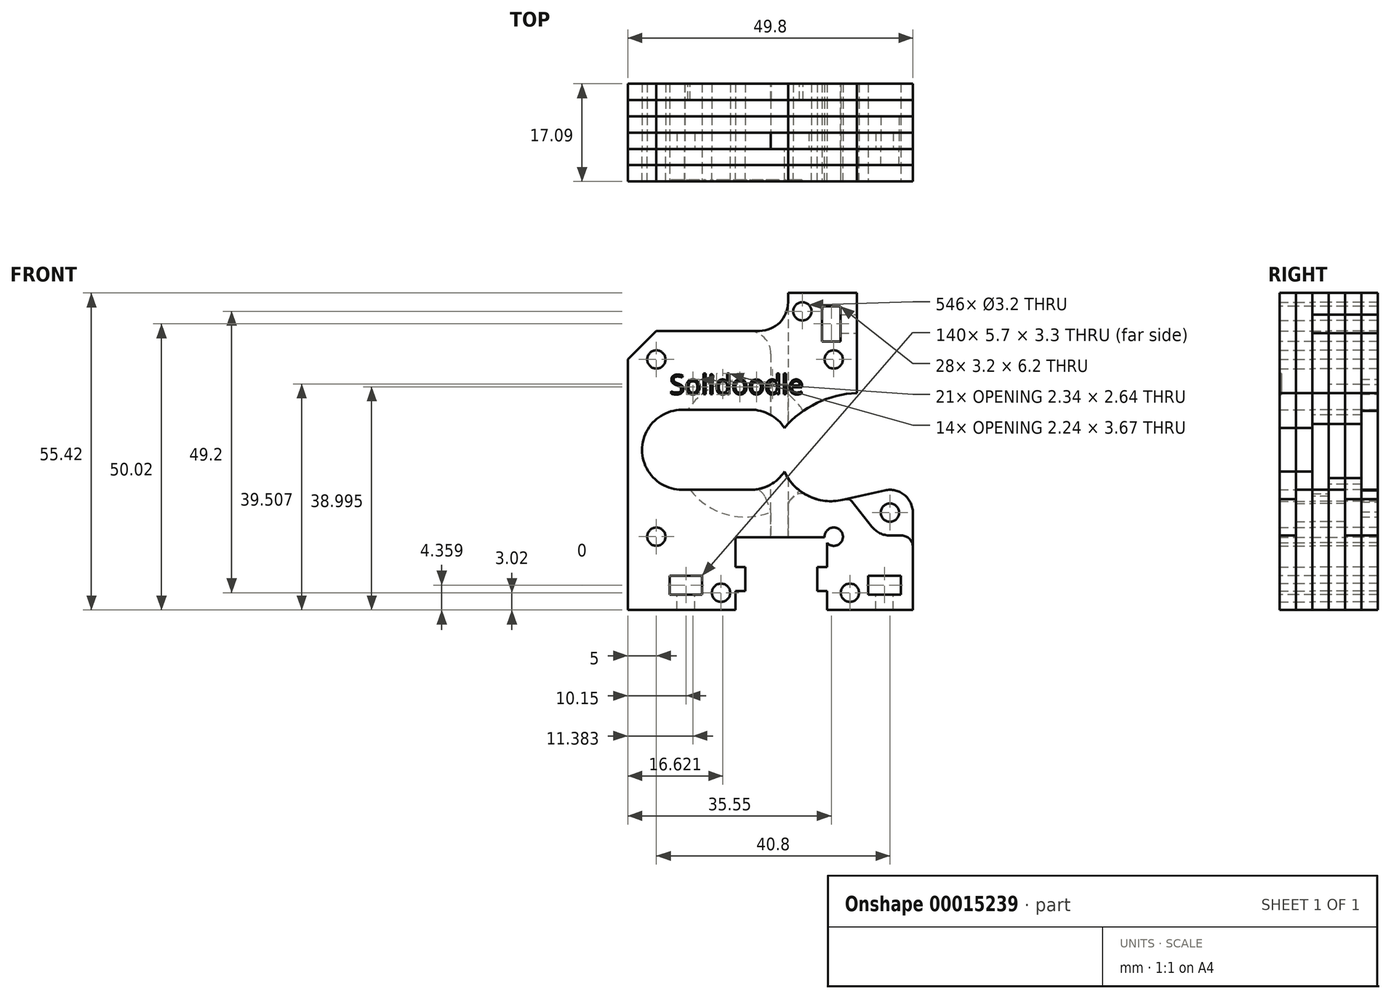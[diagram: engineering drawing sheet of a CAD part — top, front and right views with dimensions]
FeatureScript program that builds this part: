
annotation { "Feature Type Name" : "Feature", "Feature Type Description" : "" }
export const myFeature = defineFeature(function(context is Context, id is Id, definition is map)
    precondition{}
    {
        {
            var Q0;
            Q0=qCreatedBy(makeId("Front.planeOp"),FACE);
            var sketch = newSketch(context, id + "F0", { "sketchPlane" : qUnion([Q0])});
            skLineSegment(sketch, "E0.rect.left", {"start": v(-24.9, 13.58) * mm, "end": v(-24.9, -30.22) * mm});
            skLineSegment(sketch, "E0.rect.right", {"start": v(24.9, -13.2) * mm, "end": v(24.9, -30.2) * mm});
            skPoint(sketch, "E0.rect.middle", {"position": v(0, 0) * mm});
            skPoint(sketch, "E1", {"position": v(-15.4, -2.22) * mm});
            skArc(sketch, "E2", {"start": v(-15, 4.77) * mm, "mid": v(-22.4, -2.27) * mm, "end": v(-14.9, -9.2) * mm});
            skPoint(sketch, "E3", {"position": v(-3.4, -2.2) * mm});
            skArc(sketch, "E4", {"start": v(-3.4, -9.2) * mm, "mid": v(-0.07, -8.36) * mm, "end": v(2.46, -6.03) * mm});
            skLineSegment(sketch, "E5", {"start": v(-15, 4.77) * mm, "end": v(-3.4, 4.8) * mm});
            skLineSegment(sketch, "E6", {"start": v(-3.4, -9.2) * mm, "end": v(-14.9, -9.2) * mm});
            skPoint(sketch, "E7", {"position": v(10.6, -2.2) * mm});
            skArc(sketch, "E8", {"start": v(2.46, -6.03) * mm, "mid": v(6.65, -10.29) * mm, "end": v(12.58, -10.98) * mm});
            skArc(sketch, "E9.trimOffspring", {"start": v(2.46, 1.63) * mm, "mid": v(-0.09, 3.97) * mm, "end": v(-3.44, 4.8) * mm});
            skPoint(sketch, "E10", {"position": v(20.9, -13.2) * mm});
            skCircle(sketch, "E11", {"center": v(20.9, -13.2) * mm, "radius": 1.6 * mm});
            skPoint(sketch, "E12", {"position": v(24.9, -13.2) * mm});
            skLineSegment(sketch, "E13", {"start": v(15.1, 25.2) * mm, "end": v(3.1, 25.2) * mm});
            skLineSegment(sketch, "E14", {"start": v(3.1, 25.2) * mm, "end": v(3.1, 18.58) * mm});
            skLineSegment(sketch, "E15", {"start": v(3.1, 18.58) * mm, "end": v(-19.9, 18.58) * mm});
            skLineSegment(sketch, "E16.0", {"start": v(15.1, 25.2) * mm, "end": v(15.1, 7.71) * mm});
            skCircle(sketch, "E17", {"center": v(-19.9, 13.58) * mm, "radius": 1.6 * mm});
            skCircle(sketch, "E18", {"center": v(11.09, 13.58) * mm, "radius": 1.6 * mm});
            skCircle(sketch, "E19", {"center": v(-19.9, -17.4) * mm, "radius": 1.6 * mm});
            skArc(sketch, "E20", {"start": v(9.9, -18.48) * mm, "mid": v(12.56, -16.79) * mm, "end": v(9.5, -17.5) * mm});
            skCircle(sketch, "E21", {"center": v(20.9, -13.2) * mm, "radius": 4 * mm, "construction": true});
            skLineSegment(sketch, "E22", {"start": v(12.58, -10.98) * mm, "end": v(20.02, -9.3) * mm});
            skArc(sketch, "E23", {"start": v(20.02, -9.3) * mm, "mid": v(23.4, -10.08) * mm, "end": v(24.9, -13.2) * mm});
            skPoint(sketch, "E24", {"position": v(-19.9, 18.58) * mm});
            skPoint(sketch, "E25", {"position": v(-24.9, 13.58) * mm});
            skLineSegment(sketch, "E26", {"start": v(-19.9, 18.58) * mm, "end": v(-24.9, 13.58) * mm});
            skPoint(sketch, "E27.orphan", {"position": v(-24.9, 18.58) * mm});
            skPoint(sketch, "E28", {"position": v(-6.1, -30.2) * mm});
            skPoint(sketch, "E29", {"position": v(9.9, -30.2) * mm});
            skPoint(sketch, "E30.visualSharp", {"position": v(2.46, 1.63) * mm});
            skPoint(sketch, "E31.visualSharp", {"position": v(2.46, -6.03) * mm});
            skLineSegment(sketch, "E32", {"start": v(-6.1, -30.2) * mm, "end": v(-6.1, -26.9) * mm});
            skLineSegment(sketch, "E33", {"start": v(-6.1, -26.9) * mm, "end": v(-4.39, -26.9) * mm});
            skLineSegment(sketch, "E34", {"start": v(-4.39, -26.9) * mm, "end": v(-4.39, -22.7) * mm});
            skLineSegment(sketch, "E35", {"start": v(-4.39, -22.7) * mm, "end": v(-6.1, -22.7) * mm});
            skLineSegment(sketch, "E36", {"start": v(-6.1, -22.7) * mm, "end": v(-6.1, -17.5) * mm});
            skLineSegment(sketch, "E37", {"start": v(-6.1, -17.5) * mm, "end": v(1.9, -17.5) * mm});
            skLineSegment(sketch, "E38", {"start": v(1.9, -30.2) * mm, "end": v(1.9, -17.5) * mm, "construction": true});
            skLineSegment(sketch, "E39.MirrorCS", {"start": v(9.5, -17.5) * mm, "end": v(1.9, -17.5) * mm});
            skLineSegment(sketch, "E40.MirrorCS", {"start": v(9.9, -22.7) * mm, "end": v(9.9, -18.48) * mm});
            skLineSegment(sketch, "E41.MirrorCS", {"start": v(8.19, -22.7) * mm, "end": v(9.9, -22.7) * mm});
            skLineSegment(sketch, "E42.MirrorCS", {"start": v(8.19, -26.9) * mm, "end": v(8.19, -22.7) * mm});
            skLineSegment(sketch, "E43.MirrorCS", {"start": v(9.9, -26.9) * mm, "end": v(8.19, -26.9) * mm});
            skLineSegment(sketch, "E44.MirrorCS", {"start": v(9.9, -30.2) * mm, "end": v(9.9, -26.9) * mm});
            skLineSegment(sketch, "E45.trimOffspring", {"start": v(9.9, -30.2) * mm, "end": v(24.9, -30.2) * mm});
            skLineSegment(sketch, "E46", {"start": v(-24.9, -30.22) * mm, "end": v(-6.1, -30.2) * mm});
            skPoint(sketch, "E47", {"position": v(13.9, -27.2) * mm});
            skCircle(sketch, "E48", {"center": v(13.9, -27.2) * mm, "radius": 1.6 * mm});
            skPoint(sketch, "E49", {"position": v(-8.6, -27.2) * mm});
            skCircle(sketch, "E50", {"center": v(-8.6, -27.2) * mm, "radius": 1.6 * mm});
            skPoint(sketch, "E51", {"position": v(5.6, 22) * mm});
            skCircle(sketch, "E52", {"center": v(5.6, 22) * mm, "radius": 1.6 * mm});
            skArc(sketch, "E53", {"start": v(15.1, 7.71) * mm, "mid": v(8.15, 5.98) * mm, "end": v(2.46, 1.63) * mm});
            skPoint(sketch, "E54.orphan", {"position": v(9.9, -17.5) * mm});
            skSolve(sketch);
        }
        {
            var Q0;
            Q0=makeQuery(id+"F0.imprint","IMPRINT",FACE,{"disambiguationData":[TD([[makeQuery(id+"F0.imprint","IMPRINT",EDGE,{"derivedFrom":sQuery(id+"F0.wireOp",EDGE,"E0.rect.left")}),1.0]])]});
            extrude(context, id + "F1", {"entities" : qUnion([Q0]), "depth" : 2.85 * mm});
        }
        {
            var Q0;
            Q0=makeQuery(id+"F1.opExtrude","SWEPT_EDGE",EDGE,{"disambiguationData":[OSD([sQuery(id+"F0.wireOp",EDGE,"E14"),sQuery(id+"F0.wireOp",EDGE,"E15")])]});
            fillet(context, id + "F2", {"entities" : qUnion([Q0]), "radius" : 5 * mm, "tangentPropagation" : true, "allowEdgeOverflow" : false});
        }
        {
            var Q0;
            Q0=makeQuery(id+"F1.opExtrude","CAP_FACE",FACE,{"disambiguationData":[OSD([sQuery(id+"F0.wireOp",EDGE,"E0.rect.left"),sQuery(id+"F0.wireOp",EDGE,"E0.rect.right"),sQuery(id+"F0.wireOp",EDGE,"E2"),sQuery(id+"F0.wireOp",EDGE,"E4"),sQuery(id+"F0.wireOp",EDGE,"E5"),sQuery(id+"F0.wireOp",EDGE,"E6"),sQuery(id+"F0.wireOp",EDGE,"E8"),sQuery(id+"F0.wireOp",EDGE,"E9.trimOffspring"),sQuery(id+"F0.wireOp",EDGE,"E11"),sQuery(id+"F0.wireOp",EDGE,"E13"),sQuery(id+"F0.wireOp",EDGE,"E14"),sQuery(id+"F0.wireOp",EDGE,"E15"),sQuery(id+"F0.wireOp",EDGE,"E16.0"),sQuery(id+"F0.wireOp",EDGE,"E17"),sQuery(id+"F0.wireOp",EDGE,"E18"),sQuery(id+"F0.wireOp",EDGE,"E19"),sQuery(id+"F0.wireOp",EDGE,"E20"),sQuery(id+"F0.wireOp",EDGE,"E22"),sQuery(id+"F0.wireOp",EDGE,"E23"),sQuery(id+"F0.wireOp",EDGE,"E26"),sQuery(id+"F0.wireOp",EDGE,"E32"),sQuery(id+"F0.wireOp",EDGE,"E33"),sQuery(id+"F0.wireOp",EDGE,"E34"),sQuery(id+"F0.wireOp",EDGE,"E35"),sQuery(id+"F0.wireOp",EDGE,"E36"),sQuery(id+"F0.wireOp",EDGE,"E37"),sQuery(id+"F0.wireOp",EDGE,"E39.MirrorCS"),sQuery(id+"F0.wireOp",EDGE,"E40.MirrorCS"),sQuery(id+"F0.wireOp",EDGE,"E41.MirrorCS"),sQuery(id+"F0.wireOp",EDGE,"E42.MirrorCS"),sQuery(id+"F0.wireOp",EDGE,"E43.MirrorCS"),sQuery(id+"F0.wireOp",EDGE,"E44.MirrorCS"),sQuery(id+"F0.wireOp",EDGE,"E45.trimOffspring"),sQuery(id+"F0.wireOp",EDGE,"E46"),sQuery(id+"F0.wireOp",EDGE,"E48"),sQuery(id+"F0.wireOp",EDGE,"E50"),sQuery(id+"F0.wireOp",EDGE,"E52"),sQuery(id+"F0.wireOp",EDGE,"E53")])],"isStart":false});
            var sketch = newSketch(context, id + "F3", { "sketchPlane" : qUnion([Q0])});
            skLineSegment(sketch, "E55.0.0", {"start": v(-19.9, 18.58) * mm, "end": v(-24.9, 13.58) * mm});
            skLineSegment(sketch, "E55.0.1", {"start": v(-24.9, 13.58) * mm, "end": v(-24.9, -30.22) * mm});
            skLineSegment(sketch, "E55.0.2", {"start": v(-24.9, -30.22) * mm, "end": v(-6.1, -30.2) * mm});
            skLineSegment(sketch, "E55.0.3", {"start": v(-6.1, -30.2) * mm, "end": v(-6.1, -26.9) * mm});
            skLineSegment(sketch, "E55.0.4", {"start": v(-6.1, -26.9) * mm, "end": v(-4.39, -26.9) * mm});
            skLineSegment(sketch, "E55.0.5", {"start": v(-4.39, -26.9) * mm, "end": v(-4.39, -22.7) * mm});
            skLineSegment(sketch, "E55.0.6", {"start": v(-4.39, -22.7) * mm, "end": v(-6.1, -22.7) * mm});
            skLineSegment(sketch, "E55.0.7", {"start": v(-6.1, -22.7) * mm, "end": v(-6.1, -17.5) * mm});
            skLineSegment(sketch, "E55.0.8", {"start": v(-6.1, -17.5) * mm, "end": v(9.5, -17.5) * mm});
            skArc(sketch, "E55.0.9", {"start": v(9.5, -17.5) * mm, "mid": v(12.56, -16.79) * mm, "end": v(9.9, -18.48) * mm});
            skLineSegment(sketch, "E55.0.10", {"start": v(9.9, -18.48) * mm, "end": v(9.9, -22.7) * mm});
            skLineSegment(sketch, "E55.0.11", {"start": v(9.9, -22.7) * mm, "end": v(8.19, -22.7) * mm});
            skLineSegment(sketch, "E55.0.12", {"start": v(8.19, -22.7) * mm, "end": v(8.19, -26.9) * mm});
            skLineSegment(sketch, "E55.0.13", {"start": v(8.19, -26.9) * mm, "end": v(9.9, -26.9) * mm});
            skLineSegment(sketch, "E55.0.14", {"start": v(9.9, -26.9) * mm, "end": v(9.9, -30.2) * mm});
            skLineSegment(sketch, "E55.0.15", {"start": v(9.9, -30.2) * mm, "end": v(24.9, -30.2) * mm});
            skLineSegment(sketch, "E55.0.16", {"start": v(24.9, -30.2) * mm, "end": v(24.9, -13.2) * mm});
            skArc(sketch, "E55.0.17", {"start": v(24.9, -13.2) * mm, "mid": v(23.4, -10.08) * mm, "end": v(20.02, -9.3) * mm});
            skLineSegment(sketch, "E55.0.18", {"start": v(20.02, -9.3) * mm, "end": v(12.58, -10.98) * mm});
            skArc(sketch, "E55.0.19", {"start": v(12.58, -10.98) * mm, "mid": v(6.65, -10.29) * mm, "end": v(2.46, -6.03) * mm});
            skArc(sketch, "E55.0.20", {"start": v(2.46, -6.03) * mm, "mid": v(-0.07, -8.36) * mm, "end": v(-3.4, -9.2) * mm});
            skLineSegment(sketch, "E55.0.21", {"start": v(-3.4, -9.2) * mm, "end": v(-14.9, -9.2) * mm});
            skArc(sketch, "E55.0.22", {"start": v(-14.9, -9.2) * mm, "mid": v(-22.4, -2.27) * mm, "end": v(-15, 4.77) * mm});
            skLineSegment(sketch, "E55.0.23", {"start": v(-15, 4.77) * mm, "end": v(-3.44, 4.8) * mm});
            skArc(sketch, "E55.0.24", {"start": v(-3.44, 4.8) * mm, "mid": v(-0.09, 3.97) * mm, "end": v(2.46, 1.63) * mm});
            skArc(sketch, "E55.0.25", {"start": v(2.46, 1.63) * mm, "mid": v(8.15, 5.98) * mm, "end": v(15.1, 7.71) * mm});
            skLineSegment(sketch, "E55.0.26", {"start": v(15.1, 7.71) * mm, "end": v(15.1, 25.2) * mm});
            skLineSegment(sketch, "E55.0.27", {"start": v(15.1, 25.2) * mm, "end": v(3.1, 25.2) * mm});
            skLineSegment(sketch, "E55.0.28", {"start": v(3.1, 25.2) * mm, "end": v(3.1, 23.58) * mm});
            skArc(sketch, "E55.0.29", {"start": v(3.1, 23.58) * mm, "mid": v(1.64, 20.05) * mm, "end": v(-1.9, 18.58) * mm});
            skLineSegment(sketch, "E55.0.30", {"start": v(-1.9, 18.58) * mm, "end": v(-19.9, 18.58) * mm});
            skCircle(sketch, "E56.0", {"center": v(-19.9, 13.58) * mm, "radius": 1.6 * mm});
            skCircle(sketch, "E57.0", {"center": v(5.6, 22) * mm, "radius": 1.6 * mm});
            skCircle(sketch, "E58.0", {"center": v(11.09, 13.58) * mm, "radius": 1.6 * mm});
            skCircle(sketch, "E59.0", {"center": v(-19.9, -17.4) * mm, "radius": 1.6 * mm});
            skCircle(sketch, "E60.0", {"center": v(-8.6, -27.2) * mm, "radius": 1.6 * mm});
            skCircle(sketch, "E61.0", {"center": v(13.9, -27.2) * mm, "radius": 1.6 * mm});
            skCircle(sketch, "E62.0", {"center": v(20.9, -13.2) * mm, "radius": 1.6 * mm});
            skSolve(sketch);
        }
        {
            var Q0;
            Q0=makeQuery(id+"F3.imprint","IMPRINT",FACE,{"disambiguationData":[TD([[makeQuery(id+"F3.imprint","IMPRINT",EDGE,{"derivedFrom":sQuery(id+"F3.wireOp",EDGE,"E55.0.0")}),1.0]])]});
            extrude(context, id + "F4", {"entities" : qUnion([Q0]), "depth" : 2.85 * mm});
        }
        {
            var Q0;
            Q0=makeQuery(id+"F4.opExtrude","CAP_FACE",FACE,{"disambiguationData":[OSD([sQuery(id+"F3.wireOp",EDGE,"E55.0.0"),sQuery(id+"F3.wireOp",EDGE,"E55.0.1"),sQuery(id+"F3.wireOp",EDGE,"E55.0.2"),sQuery(id+"F3.wireOp",EDGE,"E55.0.3"),sQuery(id+"F3.wireOp",EDGE,"E55.0.4"),sQuery(id+"F3.wireOp",EDGE,"E55.0.5"),sQuery(id+"F3.wireOp",EDGE,"E55.0.6"),sQuery(id+"F3.wireOp",EDGE,"E55.0.7"),sQuery(id+"F3.wireOp",EDGE,"E55.0.8"),sQuery(id+"F3.wireOp",EDGE,"E55.0.9"),sQuery(id+"F3.wireOp",EDGE,"E55.0.10"),sQuery(id+"F3.wireOp",EDGE,"E55.0.11"),sQuery(id+"F3.wireOp",EDGE,"E55.0.12"),sQuery(id+"F3.wireOp",EDGE,"E55.0.13"),sQuery(id+"F3.wireOp",EDGE,"E55.0.14"),sQuery(id+"F3.wireOp",EDGE,"E55.0.15"),sQuery(id+"F3.wireOp",EDGE,"E55.0.16"),sQuery(id+"F3.wireOp",EDGE,"E55.0.17"),sQuery(id+"F3.wireOp",EDGE,"E55.0.18"),sQuery(id+"F3.wireOp",EDGE,"E55.0.19"),sQuery(id+"F3.wireOp",EDGE,"E55.0.20"),sQuery(id+"F3.wireOp",EDGE,"E55.0.21"),sQuery(id+"F3.wireOp",EDGE,"E55.0.22"),sQuery(id+"F3.wireOp",EDGE,"E55.0.23"),sQuery(id+"F3.wireOp",EDGE,"E55.0.24"),sQuery(id+"F3.wireOp",EDGE,"E55.0.25"),sQuery(id+"F3.wireOp",EDGE,"E55.0.26"),sQuery(id+"F3.wireOp",EDGE,"E55.0.27"),sQuery(id+"F3.wireOp",EDGE,"E55.0.28"),sQuery(id+"F3.wireOp",EDGE,"E55.0.29"),sQuery(id+"F3.wireOp",EDGE,"E55.0.30"),sQuery(id+"F3.wireOp",EDGE,"E56.0"),sQuery(id+"F3.wireOp",EDGE,"E57.0"),sQuery(id+"F3.wireOp",EDGE,"E58.0"),sQuery(id+"F3.wireOp",EDGE,"E59.0"),sQuery(id+"F3.wireOp",EDGE,"E60.0"),sQuery(id+"F3.wireOp",EDGE,"E61.0"),sQuery(id+"F3.wireOp",EDGE,"E62.0")])],"isStart":false});
            var sketch = newSketch(context, id + "F5", { "sketchPlane" : qUnion([Q0])});
            skText(sketch, "E63", { "text": "Solidoodle", "fontName": "OpenSans-Regular.ttf"});
            const initialGuessF5  = {"E63": [-0.01757, 0.0075, 1, 0, 0.00343]};
            skSetInitialGuess(sketch, initialGuessF5);
            skSolve(sketch);
        }
        {
            var Q0;
            Q0 = qSketchRegion(id + "F5", true);
            extrude(context, id + "F6", {"entities" : qUnion([Q0]), "operationType" : NewBodyOperationType.REMOVE, "oppositeDirection" : true, "depth" : .3 * mm});
        }
        {
            var Q0;
            Q0=makeQuery(id+"F1.opExtrude","CAP_FACE",FACE,{"disambiguationData":[OSD([sQuery(id+"F0.wireOp",EDGE,"E0.rect.left"),sQuery(id+"F0.wireOp",EDGE,"E0.rect.right"),sQuery(id+"F0.wireOp",EDGE,"E2"),sQuery(id+"F0.wireOp",EDGE,"E4"),sQuery(id+"F0.wireOp",EDGE,"E5"),sQuery(id+"F0.wireOp",EDGE,"E6"),sQuery(id+"F0.wireOp",EDGE,"E8"),sQuery(id+"F0.wireOp",EDGE,"E9.trimOffspring"),sQuery(id+"F0.wireOp",EDGE,"E11"),sQuery(id+"F0.wireOp",EDGE,"E13"),sQuery(id+"F0.wireOp",EDGE,"E14"),sQuery(id+"F0.wireOp",EDGE,"E15"),sQuery(id+"F0.wireOp",EDGE,"E16.0"),sQuery(id+"F0.wireOp",EDGE,"E17"),sQuery(id+"F0.wireOp",EDGE,"E18"),sQuery(id+"F0.wireOp",EDGE,"E19"),sQuery(id+"F0.wireOp",EDGE,"E20"),sQuery(id+"F0.wireOp",EDGE,"E22"),sQuery(id+"F0.wireOp",EDGE,"E23"),sQuery(id+"F0.wireOp",EDGE,"E26"),sQuery(id+"F0.wireOp",EDGE,"E32"),sQuery(id+"F0.wireOp",EDGE,"E33"),sQuery(id+"F0.wireOp",EDGE,"E34"),sQuery(id+"F0.wireOp",EDGE,"E35"),sQuery(id+"F0.wireOp",EDGE,"E36"),sQuery(id+"F0.wireOp",EDGE,"E37"),sQuery(id+"F0.wireOp",EDGE,"E39.MirrorCS"),sQuery(id+"F0.wireOp",EDGE,"E40.MirrorCS"),sQuery(id+"F0.wireOp",EDGE,"E41.MirrorCS"),sQuery(id+"F0.wireOp",EDGE,"E42.MirrorCS"),sQuery(id+"F0.wireOp",EDGE,"E43.MirrorCS"),sQuery(id+"F0.wireOp",EDGE,"E44.MirrorCS"),sQuery(id+"F0.wireOp",EDGE,"E45.trimOffspring"),sQuery(id+"F0.wireOp",EDGE,"E46"),sQuery(id+"F0.wireOp",EDGE,"E48"),sQuery(id+"F0.wireOp",EDGE,"E50"),sQuery(id+"F0.wireOp",EDGE,"E52"),sQuery(id+"F0.wireOp",EDGE,"E53")])],"isStart":true});
            extrude(context, id + "F7", {"entities" : qUnion([Q0]), "depth" : 2.85 * mm});
        }
        {
            var Q0;
            Q0=makeQuery(id+"F7.opExtrude","CAP_FACE",FACE,{"disambiguationData":[OSD([sQuery(id+"F0.wireOp",EDGE,"E0.rect.left"),sQuery(id+"F0.wireOp",EDGE,"E0.rect.right"),sQuery(id+"F0.wireOp",EDGE,"E2"),sQuery(id+"F0.wireOp",EDGE,"E4"),sQuery(id+"F0.wireOp",EDGE,"E5"),sQuery(id+"F0.wireOp",EDGE,"E6"),sQuery(id+"F0.wireOp",EDGE,"E8"),sQuery(id+"F0.wireOp",EDGE,"E9.trimOffspring"),sQuery(id+"F0.wireOp",EDGE,"E11"),sQuery(id+"F0.wireOp",EDGE,"E13"),sQuery(id+"F0.wireOp",EDGE,"E14"),sQuery(id+"F0.wireOp",EDGE,"E15"),sQuery(id+"F0.wireOp",EDGE,"E16.0"),sQuery(id+"F0.wireOp",EDGE,"E17"),sQuery(id+"F0.wireOp",EDGE,"E18"),sQuery(id+"F0.wireOp",EDGE,"E19"),sQuery(id+"F0.wireOp",EDGE,"E20"),sQuery(id+"F0.wireOp",EDGE,"E22"),sQuery(id+"F0.wireOp",EDGE,"E23"),sQuery(id+"F0.wireOp",EDGE,"E26"),sQuery(id+"F0.wireOp",EDGE,"E32"),sQuery(id+"F0.wireOp",EDGE,"E33"),sQuery(id+"F0.wireOp",EDGE,"E34"),sQuery(id+"F0.wireOp",EDGE,"E35"),sQuery(id+"F0.wireOp",EDGE,"E36"),sQuery(id+"F0.wireOp",EDGE,"E37"),sQuery(id+"F0.wireOp",EDGE,"E39.MirrorCS"),sQuery(id+"F0.wireOp",EDGE,"E40.MirrorCS"),sQuery(id+"F0.wireOp",EDGE,"E41.MirrorCS"),sQuery(id+"F0.wireOp",EDGE,"E42.MirrorCS"),sQuery(id+"F0.wireOp",EDGE,"E43.MirrorCS"),sQuery(id+"F0.wireOp",EDGE,"E44.MirrorCS"),sQuery(id+"F0.wireOp",EDGE,"E45.trimOffspring"),sQuery(id+"F0.wireOp",EDGE,"E46"),sQuery(id+"F0.wireOp",EDGE,"E48"),sQuery(id+"F0.wireOp",EDGE,"E50"),sQuery(id+"F0.wireOp",EDGE,"E52"),sQuery(id+"F0.wireOp",EDGE,"E53")])],"isStart":false});
            extrude(context, id + "F8", {"entities" : qUnion([Q0]), "depth" : 2.84 * mm});
        }
        {
            var Q0;
            Q0=makeQuery(id+"F8.opExtrude","CAP_FACE",FACE,{"disambiguationData":[OSD([sQuery(id+"F0.wireOp",EDGE,"E0.rect.left"),sQuery(id+"F0.wireOp",EDGE,"E0.rect.right"),sQuery(id+"F0.wireOp",EDGE,"E2"),sQuery(id+"F0.wireOp",EDGE,"E4"),sQuery(id+"F0.wireOp",EDGE,"E5"),sQuery(id+"F0.wireOp",EDGE,"E6"),sQuery(id+"F0.wireOp",EDGE,"E8"),sQuery(id+"F0.wireOp",EDGE,"E9.trimOffspring"),sQuery(id+"F0.wireOp",EDGE,"E11"),sQuery(id+"F0.wireOp",EDGE,"E13"),sQuery(id+"F0.wireOp",EDGE,"E14"),sQuery(id+"F0.wireOp",EDGE,"E15"),sQuery(id+"F0.wireOp",EDGE,"E16.0"),sQuery(id+"F0.wireOp",EDGE,"E17"),sQuery(id+"F0.wireOp",EDGE,"E18"),sQuery(id+"F0.wireOp",EDGE,"E19"),sQuery(id+"F0.wireOp",EDGE,"E20"),sQuery(id+"F0.wireOp",EDGE,"E22"),sQuery(id+"F0.wireOp",EDGE,"E23"),sQuery(id+"F0.wireOp",EDGE,"E26"),sQuery(id+"F0.wireOp",EDGE,"E32"),sQuery(id+"F0.wireOp",EDGE,"E33"),sQuery(id+"F0.wireOp",EDGE,"E34"),sQuery(id+"F0.wireOp",EDGE,"E35"),sQuery(id+"F0.wireOp",EDGE,"E36"),sQuery(id+"F0.wireOp",EDGE,"E37"),sQuery(id+"F0.wireOp",EDGE,"E39.MirrorCS"),sQuery(id+"F0.wireOp",EDGE,"E40.MirrorCS"),sQuery(id+"F0.wireOp",EDGE,"E41.MirrorCS"),sQuery(id+"F0.wireOp",EDGE,"E42.MirrorCS"),sQuery(id+"F0.wireOp",EDGE,"E43.MirrorCS"),sQuery(id+"F0.wireOp",EDGE,"E44.MirrorCS"),sQuery(id+"F0.wireOp",EDGE,"E45.trimOffspring"),sQuery(id+"F0.wireOp",EDGE,"E46"),sQuery(id+"F0.wireOp",EDGE,"E48"),sQuery(id+"F0.wireOp",EDGE,"E50"),sQuery(id+"F0.wireOp",EDGE,"E52"),sQuery(id+"F0.wireOp",EDGE,"E53")])],"isStart":false});
            var sketch = newSketch(context, id + "F9", { "sketchPlane" : qUnion([Q0])});
            skCircle(sketch, "E64.0", {"center": v(-20.9, -13.2) * mm, "radius": 1.6 * mm});
            skLineSegment(sketch, "E65.0.0", {"start": v(24.9, 13.58) * mm, "end": v(19.9, 18.58) * mm});
            skLineSegment(sketch, "E65.0.1", {"start": v(19.9, 18.58) * mm, "end": v(1.9, 18.58) * mm});
            skArc(sketch, "E65.0.2", {"start": v(1.9, 18.58) * mm, "mid": v(-1.64, 20.05) * mm, "end": v(-3.1, 23.58) * mm});
            skLineSegment(sketch, "E65.0.3", {"start": v(-3.1, 23.58) * mm, "end": v(-3.1, 25.2) * mm});
            skLineSegment(sketch, "E65.0.4", {"start": v(-3.1, 25.2) * mm, "end": v(-15.1, 25.2) * mm});
            skLineSegment(sketch, "E65.0.5", {"start": v(-15.1, 25.2) * mm, "end": v(-15.1, 7.71) * mm});
            skArc(sketch, "E65.0.6", {"start": v(-15.1, 7.71) * mm, "mid": v(-8.15, 5.98) * mm, "end": v(-2.46, 1.63) * mm});
            skArc(sketch, "E65.0.7", {"start": v(-2.46, 1.63) * mm, "mid": v(0.09, 3.97) * mm, "end": v(3.44, 4.8) * mm});
            skLineSegment(sketch, "E65.0.8", {"start": v(3.44, 4.8) * mm, "end": v(15, 4.77) * mm});
            skArc(sketch, "E65.0.9", {"start": v(15, 4.77) * mm, "mid": v(22.4, -2.27) * mm, "end": v(14.9, -9.2) * mm});
            skLineSegment(sketch, "E65.0.10", {"start": v(14.9, -9.2) * mm, "end": v(3.4, -9.2) * mm});
            skArc(sketch, "E65.0.11", {"start": v(3.4, -9.2) * mm, "mid": v(0.07, -8.36) * mm, "end": v(-2.46, -6.03) * mm});
            skArc(sketch, "E65.0.12", {"start": v(-2.46, -6.03) * mm, "mid": v(-6.65, -10.29) * mm, "end": v(-12.58, -10.98) * mm});
            skLineSegment(sketch, "E65.0.13", {"start": v(-12.58, -10.98) * mm, "end": v(-13.22, -10.83) * mm});
            skLineSegment(sketch, "E65.0.15", {"start": v(-24.9, -19.2) * mm, "end": v(-24.9, -30.2) * mm});
            skLineSegment(sketch, "E65.0.16", {"start": v(-24.9, -30.2) * mm, "end": v(-9.9, -30.2) * mm});
            skLineSegment(sketch, "E65.0.17", {"start": v(-9.9, -30.2) * mm, "end": v(-9.9, -26.9) * mm});
            skLineSegment(sketch, "E65.0.18", {"start": v(-9.9, -26.9) * mm, "end": v(-8.19, -26.9) * mm});
            skLineSegment(sketch, "E65.0.19", {"start": v(-8.19, -26.9) * mm, "end": v(-8.19, -22.7) * mm});
            skLineSegment(sketch, "E65.0.20", {"start": v(-8.19, -22.7) * mm, "end": v(-9.9, -22.7) * mm});
            skLineSegment(sketch, "E65.0.21", {"start": v(-9.9, -22.7) * mm, "end": v(-9.9, -18.48) * mm});
            skArc(sketch, "E65.0.22", {"start": v(-9.9, -18.48) * mm, "mid": v(-12.56, -16.79) * mm, "end": v(-9.5, -17.5) * mm});
            skLineSegment(sketch, "E65.0.23", {"start": v(-9.5, -17.5) * mm, "end": v(6.1, -17.5) * mm});
            skLineSegment(sketch, "E65.0.24", {"start": v(6.1, -17.5) * mm, "end": v(6.1, -22.7) * mm});
            skLineSegment(sketch, "E65.0.25", {"start": v(6.1, -22.7) * mm, "end": v(4.39, -22.7) * mm});
            skLineSegment(sketch, "E65.0.26", {"start": v(4.39, -22.7) * mm, "end": v(4.39, -26.9) * mm});
            skLineSegment(sketch, "E65.0.27", {"start": v(4.39, -26.9) * mm, "end": v(6.1, -26.9) * mm});
            skLineSegment(sketch, "E65.0.28", {"start": v(6.1, -26.9) * mm, "end": v(6.1, -30.2) * mm});
            skLineSegment(sketch, "E65.0.29", {"start": v(6.1, -30.2) * mm, "end": v(24.9, -30.22) * mm});
            skLineSegment(sketch, "E65.0.30", {"start": v(24.9, -30.22) * mm, "end": v(24.9, 13.58) * mm});
            skCircle(sketch, "E66.0", {"center": v(-13.9, -27.2) * mm, "radius": 1.6 * mm});
            skCircle(sketch, "E67.0", {"center": v(8.6, -27.2) * mm, "radius": 1.6 * mm});
            skCircle(sketch, "E68.0", {"center": v(19.9, -17.4) * mm, "radius": 1.6 * mm});
            skCircle(sketch, "E69.0", {"center": v(19.9, 13.58) * mm, "radius": 1.6 * mm});
            skCircle(sketch, "E70.0", {"center": v(-11.09, 13.58) * mm, "radius": 1.6 * mm});
            skCircle(sketch, "E71.0", {"center": v(-5.6, 22) * mm, "radius": 1.6 * mm});
            skLineSegment(sketch, "E72", {"start": v(-20.9, -17.2) * mm, "end": v(-22.9, -17.2) * mm});
            skArc(sketch, "E73.trimOffspring", {"start": v(-20.9, -17.2) * mm, "mid": v(-19.16, -16.8) * mm, "end": v(-17.76, -15.67) * mm});
            skPoint(sketch, "E74.start.orphan", {"position": v(-20.02, -9.3) * mm});
            skPoint(sketch, "E75.orphan", {"position": v(-24.9, -13.2) * mm});
            skLineSegment(sketch, "E76", {"start": v(-17.76, -15.67) * mm, "end": v(-14.23, -11.2) * mm});
            skPoint(sketch, "E77.orphan", {"position": v(-16.9, -13.2) * mm});
            skPoint(sketch, "E78.visualSharp", {"position": v(-13.84, -10.7) * mm});
            skArc(sketch, "E78.filletArc", {"start": v(-13.22, -10.83) * mm, "mid": v(-13.78, -10.87) * mm, "end": v(-14.23, -11.2) * mm});
            skPoint(sketch, "E79.visualSharp", {"position": v(-24.9, -17.2) * mm});
            skArc(sketch, "E79.filletArc", {"start": v(-22.9, -17.2) * mm, "mid": v(-24.31, -17.78) * mm, "end": v(-24.9, -19.2) * mm});
            skSolve(sketch);
        }
        {
            var Q0;
            Q0=makeQuery(id+"F9.imprint","IMPRINT",FACE,{"disambiguationData":[TD([[makeQuery(id+"F9.imprint","IMPRINT",EDGE,{"derivedFrom":sQuery(id+"F9.wireOp",EDGE,"E65.0.0")}),-1.0]])]});
            extrude(context, id + "F10", {"entities" : qUnion([Q0]), "depth" : 2.85 * mm});
        }
        {
            var Q0;
            {var subQ0=sQuery(id+"F3.wireOp",EDGE,"E55.0.0");var subQ1=sQuery(id+"F3.wireOp",EDGE,"E55.0.1");var subQ2=sQuery(id+"F3.wireOp",EDGE,"E55.0.2");var subQ3=sQuery(id+"F3.wireOp",EDGE,"E55.0.3");var subQ4=sQuery(id+"F3.wireOp",EDGE,"E55.0.4");var subQ5=sQuery(id+"F3.wireOp",EDGE,"E55.0.5");var subQ6=sQuery(id+"F3.wireOp",EDGE,"E55.0.6");var subQ7=sQuery(id+"F3.wireOp",EDGE,"E55.0.7");var subQ8=sQuery(id+"F3.wireOp",EDGE,"E55.0.8");var subQ9=sQuery(id+"F3.wireOp",EDGE,"E55.0.9");var subQ10=sQuery(id+"F3.wireOp",EDGE,"E55.0.10");var subQ11=sQuery(id+"F3.wireOp",EDGE,"E55.0.11");var subQ12=sQuery(id+"F3.wireOp",EDGE,"E55.0.12");var subQ13=sQuery(id+"F3.wireOp",EDGE,"E55.0.13");var subQ14=sQuery(id+"F3.wireOp",EDGE,"E55.0.14");var subQ15=sQuery(id+"F3.wireOp",EDGE,"E55.0.15");var subQ16=sQuery(id+"F3.wireOp",EDGE,"E55.0.16");var subQ17=sQuery(id+"F3.wireOp",EDGE,"E55.0.17");var subQ18=sQuery(id+"F3.wireOp",EDGE,"E55.0.18");var subQ19=sQuery(id+"F3.wireOp",EDGE,"E55.0.19");var subQ20=sQuery(id+"F3.wireOp",EDGE,"E55.0.20");var subQ21=sQuery(id+"F3.wireOp",EDGE,"E55.0.21");var subQ22=sQuery(id+"F3.wireOp",EDGE,"E55.0.22");var subQ23=sQuery(id+"F3.wireOp",EDGE,"E55.0.23");var subQ24=sQuery(id+"F3.wireOp",EDGE,"E55.0.24");var subQ25=sQuery(id+"F3.wireOp",EDGE,"E55.0.25");var subQ26=sQuery(id+"F3.wireOp",EDGE,"E55.0.26");var subQ27=sQuery(id+"F3.wireOp",EDGE,"E55.0.27");var subQ28=sQuery(id+"F3.wireOp",EDGE,"E55.0.28");var subQ29=sQuery(id+"F3.wireOp",EDGE,"E55.0.29");var subQ30=sQuery(id+"F3.wireOp",EDGE,"E55.0.30");var subQ31=sQuery(id+"F3.wireOp",EDGE,"E56.0");var subQ32=sQuery(id+"F3.wireOp",EDGE,"E57.0");var subQ33=sQuery(id+"F3.wireOp",EDGE,"E58.0");var subQ34=sQuery(id+"F3.wireOp",EDGE,"E59.0");var subQ35=sQuery(id+"F3.wireOp",EDGE,"E60.0");var subQ36=sQuery(id+"F3.wireOp",EDGE,"E61.0");var subQ37=sQuery(id+"F3.wireOp",EDGE,"E62.0");Q0=makeQuery(id+"F6.boolean.opBoolean","SPLIT",FACE,{"disambiguationData":[TD([makeQuery(id+"F4.opExtrude","SWEPT_FACE",FACE,{"disambiguationData":[OSD([subQ0])]})])],"derivedFrom":makeQuery(id+"F4.opExtrude","CAP_FACE",FACE,{"disambiguationData":[OSD([subQ0,subQ1,subQ2,subQ3,subQ4,subQ5,subQ6,subQ7,subQ8,subQ9,subQ10,subQ11,subQ12,subQ13,subQ14,subQ15,subQ16,subQ17,subQ18,subQ19,subQ20,subQ21,subQ22,subQ23,subQ24,subQ25,subQ26,subQ27,subQ28,subQ29,subQ30,subQ31,subQ32,subQ33,subQ34,subQ35,subQ36,subQ37])],"isStart":false})});}
            var sketch = newSketch(context, id + "F11", { "sketchPlane" : qUnion([Q0])});
            skArc(sketch, "E80.0", {"start": v(22.9, -17.2) * mm, "mid": v(24.31, -17.78) * mm, "end": v(24.9, -19.2) * mm});
            skLineSegment(sketch, "E81.0", {"start": v(20.9, -17.2) * mm, "end": v(22.9, -17.2) * mm});
            skArc(sketch, "E82.0", {"start": v(20.9, -17.2) * mm, "mid": v(19.16, -16.8) * mm, "end": v(17.76, -15.67) * mm});
            skLineSegment(sketch, "E83.0", {"start": v(17.76, -15.67) * mm, "end": v(14.23, -11.2) * mm});
            skArc(sketch, "E84.0", {"start": v(13.22, -10.83) * mm, "mid": v(13.78, -10.87) * mm, "end": v(14.23, -11.2) * mm});
            skLineSegment(sketch, "E85.0", {"start": v(13.22, -10.83) * mm, "end": v(20.02, -9.3) * mm});
            skArc(sketch, "E86.0", {"start": v(20.02, -9.3) * mm, "mid": v(23.4, -10.08) * mm, "end": v(24.9, -13.2) * mm});
            skLineSegment(sketch, "E87.0", {"start": v(24.9, -13.2) * mm, "end": v(24.9, -19.2) * mm});
            skPoint(sketch, "E88.orphan", {"position": v(24.9, -30.2) * mm});
            skPoint(sketch, "E89.orphan", {"position": v(12.58, -10.98) * mm});
            skSolve(sketch);
        }
        {
            var Q0;
            Q0 = qSketchRegion(id + "F11", true);
            extrude(context, id + "F12", {"entities" : qUnion([Q0]), "operationType" : NewBodyOperationType.REMOVE, "oppositeDirection" : true, "depth" : 2.85 * mm});
        }
        {
            var Q0;
            Q0=makeQuery(id+"F10.opExtrude","CAP_FACE",FACE,{"disambiguationData":[OSD([sQuery(id+"F9.wireOp",EDGE,"E65.0.0"),sQuery(id+"F9.wireOp",EDGE,"E65.0.1"),sQuery(id+"F9.wireOp",EDGE,"E65.0.2"),sQuery(id+"F9.wireOp",EDGE,"E65.0.3"),sQuery(id+"F9.wireOp",EDGE,"E65.0.4"),sQuery(id+"F9.wireOp",EDGE,"E65.0.5"),sQuery(id+"F9.wireOp",EDGE,"E65.0.6"),sQuery(id+"F9.wireOp",EDGE,"E65.0.7"),sQuery(id+"F9.wireOp",EDGE,"E65.0.8"),sQuery(id+"F9.wireOp",EDGE,"E65.0.9"),sQuery(id+"F9.wireOp",EDGE,"E65.0.10"),sQuery(id+"F9.wireOp",EDGE,"E65.0.11"),sQuery(id+"F9.wireOp",EDGE,"E65.0.12"),sQuery(id+"F9.wireOp",EDGE,"E65.0.13"),sQuery(id+"F9.wireOp",EDGE,"E65.0.15"),sQuery(id+"F9.wireOp",EDGE,"E65.0.16"),sQuery(id+"F9.wireOp",EDGE,"E65.0.17"),sQuery(id+"F9.wireOp",EDGE,"E65.0.18"),sQuery(id+"F9.wireOp",EDGE,"E65.0.19"),sQuery(id+"F9.wireOp",EDGE,"E65.0.20"),sQuery(id+"F9.wireOp",EDGE,"E65.0.21"),sQuery(id+"F9.wireOp",EDGE,"E65.0.22"),sQuery(id+"F9.wireOp",EDGE,"E65.0.23"),sQuery(id+"F9.wireOp",EDGE,"E65.0.24"),sQuery(id+"F9.wireOp",EDGE,"E65.0.25"),sQuery(id+"F9.wireOp",EDGE,"E65.0.26"),sQuery(id+"F9.wireOp",EDGE,"E65.0.27"),sQuery(id+"F9.wireOp",EDGE,"E65.0.28"),sQuery(id+"F9.wireOp",EDGE,"E65.0.29"),sQuery(id+"F9.wireOp",EDGE,"E65.0.30"),sQuery(id+"F9.wireOp",EDGE,"E66.0"),sQuery(id+"F9.wireOp",EDGE,"E67.0"),sQuery(id+"F9.wireOp",EDGE,"E68.0"),sQuery(id+"F9.wireOp",EDGE,"E69.0"),sQuery(id+"F9.wireOp",EDGE,"E70.0"),sQuery(id+"F9.wireOp",EDGE,"E71.0"),sQuery(id+"F9.wireOp",EDGE,"E72"),sQuery(id+"F9.wireOp",EDGE,"E73.trimOffspring"),sQuery(id+"F9.wireOp",EDGE,"E76"),sQuery(id+"F9.wireOp",EDGE,"E78.filletArc"),sQuery(id+"F9.wireOp",EDGE,"E79.filletArc")])],"isStart":false});
            extrude(context, id + "F13", {"entities" : qUnion([Q0]), "depth" : 2.85 * mm});
        }
        {
            var Q0;
            Q0=makeQuery(id+"F13.opExtrude","CAP_FACE",FACE,{"disambiguationData":[OSD([sQuery(id+"F9.wireOp",EDGE,"E65.0.0"),sQuery(id+"F9.wireOp",EDGE,"E65.0.1"),sQuery(id+"F9.wireOp",EDGE,"E65.0.2"),sQuery(id+"F9.wireOp",EDGE,"E65.0.3"),sQuery(id+"F9.wireOp",EDGE,"E65.0.4"),sQuery(id+"F9.wireOp",EDGE,"E65.0.5"),sQuery(id+"F9.wireOp",EDGE,"E65.0.6"),sQuery(id+"F9.wireOp",EDGE,"E65.0.7"),sQuery(id+"F9.wireOp",EDGE,"E65.0.8"),sQuery(id+"F9.wireOp",EDGE,"E65.0.9"),sQuery(id+"F9.wireOp",EDGE,"E65.0.10"),sQuery(id+"F9.wireOp",EDGE,"E65.0.11"),sQuery(id+"F9.wireOp",EDGE,"E65.0.12"),sQuery(id+"F9.wireOp",EDGE,"E65.0.13"),sQuery(id+"F9.wireOp",EDGE,"E65.0.15"),sQuery(id+"F9.wireOp",EDGE,"E65.0.16"),sQuery(id+"F9.wireOp",EDGE,"E65.0.17"),sQuery(id+"F9.wireOp",EDGE,"E65.0.18"),sQuery(id+"F9.wireOp",EDGE,"E65.0.19"),sQuery(id+"F9.wireOp",EDGE,"E65.0.20"),sQuery(id+"F9.wireOp",EDGE,"E65.0.21"),sQuery(id+"F9.wireOp",EDGE,"E65.0.22"),sQuery(id+"F9.wireOp",EDGE,"E65.0.23"),sQuery(id+"F9.wireOp",EDGE,"E65.0.24"),sQuery(id+"F9.wireOp",EDGE,"E65.0.25"),sQuery(id+"F9.wireOp",EDGE,"E65.0.26"),sQuery(id+"F9.wireOp",EDGE,"E65.0.27"),sQuery(id+"F9.wireOp",EDGE,"E65.0.28"),sQuery(id+"F9.wireOp",EDGE,"E65.0.29"),sQuery(id+"F9.wireOp",EDGE,"E65.0.30"),sQuery(id+"F9.wireOp",EDGE,"E66.0"),sQuery(id+"F9.wireOp",EDGE,"E67.0"),sQuery(id+"F9.wireOp",EDGE,"E68.0"),sQuery(id+"F9.wireOp",EDGE,"E69.0"),sQuery(id+"F9.wireOp",EDGE,"E70.0"),sQuery(id+"F9.wireOp",EDGE,"E71.0"),sQuery(id+"F9.wireOp",EDGE,"E72"),sQuery(id+"F9.wireOp",EDGE,"E73.trimOffspring"),sQuery(id+"F9.wireOp",EDGE,"E76"),sQuery(id+"F9.wireOp",EDGE,"E78.filletArc"),sQuery(id+"F9.wireOp",EDGE,"E79.filletArc")])],"isStart":false});
            var sketch = newSketch(context, id + "F14", { "sketchPlane" : qUnion([Q0])});
            skCircle(sketch, "E90.0", {"center": v(-11.09, 13.58) * mm, "radius": 1.6 * mm, "construction": true});
            skCircle(sketch, "E91.0", {"center": v(19.9, 13.58) * mm, "radius": 1.6 * mm, "construction": true});
            skCircle(sketch, "E92.0", {"center": v(19.9, -17.4) * mm, "radius": 1.6 * mm, "construction": true});
            skArc(sketch, "E93.0", {"start": v(-9.9, -18.48) * mm, "mid": v(-12.56, -16.79) * mm, "end": v(-9.5, -17.5) * mm, "construction": true});
            skLineSegment(sketch, "E94", {"start": v(-11.09, 13.58) * mm, "end": v(19.9, -17.4) * mm, "construction": true});
            skLineSegment(sketch, "E95", {"start": v(19.9, 13.58) * mm, "end": v(-11.09, -17.4) * mm, "construction": true});
            skCircle(sketch, "E96", {"center": v(4.4, -1.91) * mm, "radius": 12.05 * mm});
            skSolve(sketch);
        }
        {
            var Q0;
            Q0 = qSketchRegion(id + "F14", true);
            extrude(context, id + "F15", {"entities" : qUnion([Q0]), "operationType" : NewBodyOperationType.REMOVE, "oppositeDirection" : true, "depth" : 2.85 * mm});
        }
        {
            var Q0;
            Q0=makeQuery(id+"F7.opExtrude","CAP_FACE",FACE,{"disambiguationData":[OSD([sQuery(id+"F0.wireOp",EDGE,"E0.rect.left"),sQuery(id+"F0.wireOp",EDGE,"E0.rect.right"),sQuery(id+"F0.wireOp",EDGE,"E2"),sQuery(id+"F0.wireOp",EDGE,"E4"),sQuery(id+"F0.wireOp",EDGE,"E5"),sQuery(id+"F0.wireOp",EDGE,"E6"),sQuery(id+"F0.wireOp",EDGE,"E8"),sQuery(id+"F0.wireOp",EDGE,"E9.trimOffspring"),sQuery(id+"F0.wireOp",EDGE,"E11"),sQuery(id+"F0.wireOp",EDGE,"E13"),sQuery(id+"F0.wireOp",EDGE,"E14"),sQuery(id+"F0.wireOp",EDGE,"E15"),sQuery(id+"F0.wireOp",EDGE,"E16.0"),sQuery(id+"F0.wireOp",EDGE,"E17"),sQuery(id+"F0.wireOp",EDGE,"E18"),sQuery(id+"F0.wireOp",EDGE,"E19"),sQuery(id+"F0.wireOp",EDGE,"E20"),sQuery(id+"F0.wireOp",EDGE,"E22"),sQuery(id+"F0.wireOp",EDGE,"E23"),sQuery(id+"F0.wireOp",EDGE,"E26"),sQuery(id+"F0.wireOp",EDGE,"E32"),sQuery(id+"F0.wireOp",EDGE,"E33"),sQuery(id+"F0.wireOp",EDGE,"E34"),sQuery(id+"F0.wireOp",EDGE,"E35"),sQuery(id+"F0.wireOp",EDGE,"E36"),sQuery(id+"F0.wireOp",EDGE,"E37"),sQuery(id+"F0.wireOp",EDGE,"E39.MirrorCS"),sQuery(id+"F0.wireOp",EDGE,"E40.MirrorCS"),sQuery(id+"F0.wireOp",EDGE,"E41.MirrorCS"),sQuery(id+"F0.wireOp",EDGE,"E42.MirrorCS"),sQuery(id+"F0.wireOp",EDGE,"E43.MirrorCS"),sQuery(id+"F0.wireOp",EDGE,"E44.MirrorCS"),sQuery(id+"F0.wireOp",EDGE,"E45.trimOffspring"),sQuery(id+"F0.wireOp",EDGE,"E46"),sQuery(id+"F0.wireOp",EDGE,"E48"),sQuery(id+"F0.wireOp",EDGE,"E50"),sQuery(id+"F0.wireOp",EDGE,"E52"),sQuery(id+"F0.wireOp",EDGE,"E53")])],"isStart":true});
            var sketch = newSketch(context, id + "F16", { "sketchPlane" : qUnion([Q0])});
            skLineSegment(sketch, "E97.bottom", {"start": v(3.1, 23.58) * mm, "end": v(0.1, 23.58) * mm});
            skLineSegment(sketch, "E97.top", {"start": v(3.1, 0) * mm, "end": v(0.1, 0) * mm});
            skLineSegment(sketch, "E97.left", {"start": v(3.1, 23.58) * mm, "end": v(3.1, 0) * mm});
            skLineSegment(sketch, "E97.right", {"start": v(0.1, 23.58) * mm, "end": v(0.1, 0) * mm});
            skSolve(sketch);
        }
        {
            var Q0;
            Q0 = qSketchRegion(id + "F16", true);
            extrude(context, id + "F17", {"entities" : qUnion([Q0]), "operationType" : NewBodyOperationType.REMOVE, "oppositeDirection" : true, "depth" : 2.85 * mm});
        }
        {
            var Q0;
            Q0=makeQuery(id+"F17.boolean.opBoolean","INTERSECT",EDGE,{"derivedFrom":[makeQuery(id+"F7.opExtrude","SWEPT_FACE",FACE,{"disambiguationData":[OSD([sQuery(id+"F0.wireOp",EDGE,"E0.rect.left"),sQuery(id+"F0.wireOp",EDGE,"E0.rect.right"),sQuery(id+"F0.wireOp",EDGE,"E2"),sQuery(id+"F0.wireOp",EDGE,"E4"),sQuery(id+"F0.wireOp",EDGE,"E5"),sQuery(id+"F0.wireOp",EDGE,"E6"),sQuery(id+"F0.wireOp",EDGE,"E8"),sQuery(id+"F0.wireOp",EDGE,"E9.trimOffspring"),sQuery(id+"F0.wireOp",EDGE,"E11"),sQuery(id+"F0.wireOp",EDGE,"E13"),sQuery(id+"F0.wireOp",EDGE,"E14"),sQuery(id+"F0.wireOp",EDGE,"E15"),sQuery(id+"F0.wireOp",EDGE,"E16.0"),sQuery(id+"F0.wireOp",EDGE,"E17"),sQuery(id+"F0.wireOp",EDGE,"E18"),sQuery(id+"F0.wireOp",EDGE,"E19"),sQuery(id+"F0.wireOp",EDGE,"E20"),sQuery(id+"F0.wireOp",EDGE,"E22"),sQuery(id+"F0.wireOp",EDGE,"E23"),sQuery(id+"F0.wireOp",EDGE,"E26"),sQuery(id+"F0.wireOp",EDGE,"E32"),sQuery(id+"F0.wireOp",EDGE,"E33"),sQuery(id+"F0.wireOp",EDGE,"E34"),sQuery(id+"F0.wireOp",EDGE,"E35"),sQuery(id+"F0.wireOp",EDGE,"E36"),sQuery(id+"F0.wireOp",EDGE,"E37"),sQuery(id+"F0.wireOp",EDGE,"E39.MirrorCS"),sQuery(id+"F0.wireOp",EDGE,"E40.MirrorCS"),sQuery(id+"F0.wireOp",EDGE,"E41.MirrorCS"),sQuery(id+"F0.wireOp",EDGE,"E42.MirrorCS"),sQuery(id+"F0.wireOp",EDGE,"E43.MirrorCS"),sQuery(id+"F0.wireOp",EDGE,"E44.MirrorCS"),sQuery(id+"F0.wireOp",EDGE,"E45.trimOffspring"),sQuery(id+"F0.wireOp",EDGE,"E46"),sQuery(id+"F0.wireOp",EDGE,"E48"),sQuery(id+"F0.wireOp",EDGE,"E50"),sQuery(id+"F0.wireOp",EDGE,"E52"),sQuery(id+"F0.wireOp",EDGE,"E53")])]}),makeQuery(id+"F17.opExtrude","SWEPT_FACE",FACE,{"disambiguationData":[OSD([sQuery(id+"F16.wireOp",EDGE,"E97.right")])]})]});
            fillet(context, id + "F18", {"entities" : qUnion([Q0]), "radius" : 4 * mm, "tangentPropagation" : true, "allowEdgeOverflow" : false});
        }
        {
            var Q0;
            {var subQ0=sQuery(id+"F3.wireOp",EDGE,"E55.0.0");var subQ1=sQuery(id+"F3.wireOp",EDGE,"E55.0.1");var subQ2=sQuery(id+"F3.wireOp",EDGE,"E55.0.2");var subQ3=sQuery(id+"F3.wireOp",EDGE,"E55.0.3");var subQ4=sQuery(id+"F3.wireOp",EDGE,"E55.0.4");var subQ5=sQuery(id+"F3.wireOp",EDGE,"E55.0.5");var subQ6=sQuery(id+"F3.wireOp",EDGE,"E55.0.6");var subQ7=sQuery(id+"F3.wireOp",EDGE,"E55.0.7");var subQ8=sQuery(id+"F3.wireOp",EDGE,"E55.0.8");var subQ9=sQuery(id+"F3.wireOp",EDGE,"E55.0.9");var subQ10=sQuery(id+"F3.wireOp",EDGE,"E55.0.10");var subQ11=sQuery(id+"F3.wireOp",EDGE,"E55.0.11");var subQ12=sQuery(id+"F3.wireOp",EDGE,"E55.0.12");var subQ13=sQuery(id+"F3.wireOp",EDGE,"E55.0.13");var subQ14=sQuery(id+"F3.wireOp",EDGE,"E55.0.14");var subQ15=sQuery(id+"F3.wireOp",EDGE,"E55.0.15");var subQ16=sQuery(id+"F3.wireOp",EDGE,"E55.0.16");var subQ17=sQuery(id+"F3.wireOp",EDGE,"E55.0.17");var subQ18=sQuery(id+"F3.wireOp",EDGE,"E55.0.18");var subQ19=sQuery(id+"F3.wireOp",EDGE,"E55.0.19");var subQ20=sQuery(id+"F3.wireOp",EDGE,"E55.0.20");var subQ21=sQuery(id+"F3.wireOp",EDGE,"E55.0.21");var subQ22=sQuery(id+"F3.wireOp",EDGE,"E55.0.22");var subQ23=sQuery(id+"F3.wireOp",EDGE,"E55.0.23");var subQ24=sQuery(id+"F3.wireOp",EDGE,"E55.0.24");var subQ25=sQuery(id+"F3.wireOp",EDGE,"E55.0.25");var subQ26=sQuery(id+"F3.wireOp",EDGE,"E55.0.26");var subQ27=sQuery(id+"F3.wireOp",EDGE,"E55.0.27");var subQ28=sQuery(id+"F3.wireOp",EDGE,"E55.0.28");var subQ29=sQuery(id+"F3.wireOp",EDGE,"E55.0.29");var subQ30=sQuery(id+"F3.wireOp",EDGE,"E55.0.30");var subQ31=sQuery(id+"F3.wireOp",EDGE,"E56.0");var subQ32=sQuery(id+"F3.wireOp",EDGE,"E57.0");var subQ33=sQuery(id+"F3.wireOp",EDGE,"E58.0");var subQ34=sQuery(id+"F3.wireOp",EDGE,"E59.0");var subQ35=sQuery(id+"F3.wireOp",EDGE,"E60.0");var subQ36=sQuery(id+"F3.wireOp",EDGE,"E61.0");var subQ37=sQuery(id+"F3.wireOp",EDGE,"E62.0");Q0=makeQuery(id+"F6.boolean.opBoolean","SPLIT",FACE,{"disambiguationData":[TD([makeQuery(id+"F4.opExtrude","SWEPT_FACE",FACE,{"disambiguationData":[OSD([subQ0])]})])],"derivedFrom":makeQuery(id+"F4.opExtrude","CAP_FACE",FACE,{"disambiguationData":[OSD([subQ0,subQ1,subQ2,subQ3,subQ4,subQ5,subQ6,subQ7,subQ8,subQ9,subQ10,subQ11,subQ12,subQ13,subQ14,subQ15,subQ16,subQ17,subQ18,subQ19,subQ20,subQ21,subQ22,subQ23,subQ24,subQ25,subQ26,subQ27,subQ28,subQ29,subQ30,subQ31,subQ32,subQ33,subQ34,subQ35,subQ36,subQ37])],"isStart":false})});}
            var sketch = newSketch(context, id + "F19", { "sketchPlane" : qUnion([Q0])});
            skLineSegment(sketch, "E98.bottom", {"start": v(-17.6, -24.21) * mm, "end": v(-11.9, -24.21) * mm});
            skLineSegment(sketch, "E98.top", {"start": v(-17.6, -27.51) * mm, "end": v(-11.9, -27.51) * mm});
            skLineSegment(sketch, "E98.left", {"start": v(-17.6, -24.21) * mm, "end": v(-17.6, -27.51) * mm});
            skLineSegment(sketch, "E98.right", {"start": v(-11.9, -24.21) * mm, "end": v(-11.9, -27.51) * mm});
            skLineSegment(sketch, "E99.bottom", {"start": v(17.1, -24.21) * mm, "end": v(22.8, -24.21) * mm});
            skLineSegment(sketch, "E99.top", {"start": v(17.1, -27.51) * mm, "end": v(22.8, -27.51) * mm});
            skLineSegment(sketch, "E99.left", {"start": v(17.1, -24.21) * mm, "end": v(17.1, -27.51) * mm});
            skLineSegment(sketch, "E99.right", {"start": v(22.8, -24.21) * mm, "end": v(22.8, -27.51) * mm});
            skSolve(sketch);
        }
        {
            var Q0;
            Q0 = qSketchRegion(id + "F19", true);
            extrude(context, id + "F20", {"entities" : qUnion([Q0]), "operationType" : NewBodyOperationType.REMOVE, "oppositeDirection" : true, "depth" : 25 * mm});
        }
        {
            var Q0;
            {var subQ0=sQuery(id+"F0.wireOp",EDGE,"E0.rect.left");var subQ1=sQuery(id+"F0.wireOp",EDGE,"E0.rect.right");var subQ2=sQuery(id+"F0.wireOp",EDGE,"E2");var subQ3=sQuery(id+"F0.wireOp",EDGE,"E4");var subQ4=sQuery(id+"F0.wireOp",EDGE,"E5");var subQ5=sQuery(id+"F0.wireOp",EDGE,"E6");var subQ6=sQuery(id+"F0.wireOp",EDGE,"E8");var subQ7=sQuery(id+"F0.wireOp",EDGE,"E9.trimOffspring");var subQ8=sQuery(id+"F0.wireOp",EDGE,"E11");var subQ9=sQuery(id+"F0.wireOp",EDGE,"E13");var subQ10=sQuery(id+"F0.wireOp",EDGE,"E14");var subQ11=sQuery(id+"F0.wireOp",EDGE,"E15");var subQ12=sQuery(id+"F0.wireOp",EDGE,"E16.0");var subQ13=sQuery(id+"F0.wireOp",EDGE,"E17");var subQ14=sQuery(id+"F0.wireOp",EDGE,"E18");var subQ15=sQuery(id+"F0.wireOp",EDGE,"E19");var subQ16=sQuery(id+"F0.wireOp",EDGE,"E20");var subQ17=sQuery(id+"F0.wireOp",EDGE,"E22");var subQ18=sQuery(id+"F0.wireOp",EDGE,"E23");var subQ19=sQuery(id+"F0.wireOp",EDGE,"E26");var subQ20=sQuery(id+"F0.wireOp",EDGE,"E32");var subQ21=sQuery(id+"F0.wireOp",EDGE,"E33");var subQ22=sQuery(id+"F0.wireOp",EDGE,"E34");var subQ23=sQuery(id+"F0.wireOp",EDGE,"E35");var subQ24=sQuery(id+"F0.wireOp",EDGE,"E36");var subQ25=sQuery(id+"F0.wireOp",EDGE,"E37");var subQ26=sQuery(id+"F0.wireOp",EDGE,"E39.MirrorCS");var subQ27=sQuery(id+"F0.wireOp",EDGE,"E40.MirrorCS");var subQ28=sQuery(id+"F0.wireOp",EDGE,"E41.MirrorCS");var subQ29=sQuery(id+"F0.wireOp",EDGE,"E42.MirrorCS");var subQ30=sQuery(id+"F0.wireOp",EDGE,"E43.MirrorCS");var subQ31=sQuery(id+"F0.wireOp",EDGE,"E44.MirrorCS");var subQ32=sQuery(id+"F0.wireOp",EDGE,"E45.trimOffspring");var subQ33=sQuery(id+"F0.wireOp",EDGE,"E46");var subQ34=sQuery(id+"F0.wireOp",EDGE,"E48");var subQ35=sQuery(id+"F0.wireOp",EDGE,"E50");var subQ36=sQuery(id+"F0.wireOp",EDGE,"E52");var subQ37=sQuery(id+"F0.wireOp",EDGE,"E53");Q0=makeQuery(id+"F17.boolean.opBoolean","SPLIT",FACE,{"disambiguationData":[TD([makeQuery(id+"F7.opExtrude","SWEPT_FACE",FACE,{"disambiguationData":[OSD([subQ0])]})])],"derivedFrom":makeQuery(id+"F7.opExtrude","CAP_FACE",FACE,{"disambiguationData":[OSD([subQ0,subQ1,subQ2,subQ3,subQ4,subQ5,subQ6,subQ7,subQ8,subQ9,subQ10,subQ11,subQ12,subQ13,subQ14,subQ15,subQ16,subQ17,subQ18,subQ19,subQ20,subQ21,subQ22,subQ23,subQ24,subQ25,subQ26,subQ27,subQ28,subQ29,subQ30,subQ31,subQ32,subQ33,subQ34,subQ35,subQ36,subQ37])],"isStart":true})});}
            var sketch = newSketch(context, id + "F21", { "sketchPlane" : qUnion([Q0])});
            skLineSegment(sketch, "E100.0", {"start": v(-17.6, -24.21) * mm, "end": v(-17.6, -27.51) * mm, "construction": true});
            skLineSegment(sketch, "E101.0", {"start": v(-11.9, -24.21) * mm, "end": v(-11.9, -27.51) * mm, "construction": true});
            skLineSegment(sketch, "E102.0", {"start": v(17.1, -24.21) * mm, "end": v(17.1, -27.51) * mm, "construction": true});
            skLineSegment(sketch, "E103.0", {"start": v(22.8, -24.21) * mm, "end": v(22.8, -27.51) * mm, "construction": true});
            skLineSegment(sketch, "E104", {"start": v(-17.6, -27.51) * mm, "end": v(-11.9, -27.51) * mm, "construction": true});
            skLineSegment(sketch, "E105", {"start": v(17.1, -27.51) * mm, "end": v(22.8, -27.51) * mm, "construction": true});
            skLineSegment(sketch, "E106", {"start": v(-14.75, -27.51) * mm, "end": v(-14.75, -30.2) * mm, "construction": true});
            skLineSegment(sketch, "E107", {"start": v(19.95, -27.51) * mm, "end": v(19.95, -30.2) * mm, "construction": true});
            skLineSegment(sketch, "E108.rect.bottom", {"start": v(21.5, -30.64) * mm, "end": v(18.4, -30.64) * mm});
            skLineSegment(sketch, "E108.rect.top", {"start": v(21.5, -24.38) * mm, "end": v(18.4, -24.38) * mm});
            skLineSegment(sketch, "E108.rect.left", {"start": v(21.5, -30.64) * mm, "end": v(21.5, -24.38) * mm});
            skLineSegment(sketch, "E108.rect.right", {"start": v(18.4, -30.64) * mm, "end": v(18.4, -24.38) * mm});
            skPoint(sketch, "E108.rect.middle", {"position": v(19.95, -27.51) * mm});
            skLineSegment(sketch, "E109.rect.bottom", {"start": v(-13.2, -30.55) * mm, "end": v(-16.3, -30.55) * mm});
            skLineSegment(sketch, "E109.rect.top", {"start": v(-13.2, -24.47) * mm, "end": v(-16.3, -24.47) * mm});
            skLineSegment(sketch, "E109.rect.left", {"start": v(-13.2, -30.55) * mm, "end": v(-13.2, -24.47) * mm});
            skLineSegment(sketch, "E109.rect.right", {"start": v(-16.3, -30.55) * mm, "end": v(-16.3, -24.47) * mm});
            skPoint(sketch, "E109.rect.middle", {"position": v(-14.75, -27.51) * mm});
            skSolve(sketch);
        }
        {
            var Q0;
            Q0 = qSketchRegion(id + "F21", true);
            extrude(context, id + "F22", {"entities" : qUnion([Q0]), "operationType" : NewBodyOperationType.REMOVE, "oppositeDirection" : true, "depth" : 2.85 * mm});
        }
        {
            var Q0;
            {var subQ0=sQuery(id+"F3.wireOp",EDGE,"E55.0.0");var subQ1=sQuery(id+"F3.wireOp",EDGE,"E55.0.1");var subQ2=sQuery(id+"F3.wireOp",EDGE,"E55.0.2");var subQ3=sQuery(id+"F3.wireOp",EDGE,"E55.0.3");var subQ4=sQuery(id+"F3.wireOp",EDGE,"E55.0.4");var subQ5=sQuery(id+"F3.wireOp",EDGE,"E55.0.5");var subQ6=sQuery(id+"F3.wireOp",EDGE,"E55.0.6");var subQ7=sQuery(id+"F3.wireOp",EDGE,"E55.0.7");var subQ8=sQuery(id+"F3.wireOp",EDGE,"E55.0.8");var subQ9=sQuery(id+"F3.wireOp",EDGE,"E55.0.9");var subQ10=sQuery(id+"F3.wireOp",EDGE,"E55.0.10");var subQ11=sQuery(id+"F3.wireOp",EDGE,"E55.0.11");var subQ12=sQuery(id+"F3.wireOp",EDGE,"E55.0.12");var subQ13=sQuery(id+"F3.wireOp",EDGE,"E55.0.13");var subQ14=sQuery(id+"F3.wireOp",EDGE,"E55.0.14");var subQ15=sQuery(id+"F3.wireOp",EDGE,"E55.0.15");var subQ16=sQuery(id+"F3.wireOp",EDGE,"E55.0.16");var subQ17=sQuery(id+"F3.wireOp",EDGE,"E55.0.17");var subQ18=sQuery(id+"F3.wireOp",EDGE,"E55.0.18");var subQ19=sQuery(id+"F3.wireOp",EDGE,"E55.0.19");var subQ20=sQuery(id+"F3.wireOp",EDGE,"E55.0.20");var subQ21=sQuery(id+"F3.wireOp",EDGE,"E55.0.21");var subQ22=sQuery(id+"F3.wireOp",EDGE,"E55.0.22");var subQ23=sQuery(id+"F3.wireOp",EDGE,"E55.0.23");var subQ24=sQuery(id+"F3.wireOp",EDGE,"E55.0.24");var subQ25=sQuery(id+"F3.wireOp",EDGE,"E55.0.25");var subQ26=sQuery(id+"F3.wireOp",EDGE,"E55.0.26");var subQ27=sQuery(id+"F3.wireOp",EDGE,"E55.0.27");var subQ28=sQuery(id+"F3.wireOp",EDGE,"E55.0.28");var subQ29=sQuery(id+"F3.wireOp",EDGE,"E55.0.29");var subQ30=sQuery(id+"F3.wireOp",EDGE,"E55.0.30");var subQ31=sQuery(id+"F3.wireOp",EDGE,"E56.0");var subQ32=sQuery(id+"F3.wireOp",EDGE,"E57.0");var subQ33=sQuery(id+"F3.wireOp",EDGE,"E58.0");var subQ34=sQuery(id+"F3.wireOp",EDGE,"E59.0");var subQ35=sQuery(id+"F3.wireOp",EDGE,"E60.0");var subQ36=sQuery(id+"F3.wireOp",EDGE,"E61.0");var subQ37=sQuery(id+"F3.wireOp",EDGE,"E62.0");Q0=makeQuery(id+"F6.boolean.opBoolean","SPLIT",FACE,{"disambiguationData":[TD([makeQuery(id+"F4.opExtrude","SWEPT_FACE",FACE,{"disambiguationData":[OSD([subQ0])]})])],"derivedFrom":makeQuery(id+"F4.opExtrude","CAP_FACE",FACE,{"disambiguationData":[OSD([subQ0,subQ1,subQ2,subQ3,subQ4,subQ5,subQ6,subQ7,subQ8,subQ9,subQ10,subQ11,subQ12,subQ13,subQ14,subQ15,subQ16,subQ17,subQ18,subQ19,subQ20,subQ21,subQ22,subQ23,subQ24,subQ25,subQ26,subQ27,subQ28,subQ29,subQ30,subQ31,subQ32,subQ33,subQ34,subQ35,subQ36,subQ37])],"isStart":false})});}
            var sketch = newSketch(context, id + "F23", { "sketchPlane" : qUnion([Q0])});
            skLineSegment(sketch, "E110.bottom", {"start": v(9.05, 22.9) * mm, "end": v(12.25, 22.9) * mm});
            skLineSegment(sketch, "E110.top", {"start": v(9.05, 16.7) * mm, "end": v(12.25, 16.7) * mm});
            skLineSegment(sketch, "E110.left", {"start": v(9.05, 22.9) * mm, "end": v(9.05, 16.7) * mm});
            skLineSegment(sketch, "E110.right", {"start": v(12.25, 22.9) * mm, "end": v(12.25, 16.7) * mm});
            skSolve(sketch);
        }
        {
            var Q0;
            Q0 = qSketchRegion(id + "F23", true);
            extrude(context, id + "F24", {"entities" : qUnion([Q0]), "operationType" : NewBodyOperationType.REMOVE, "oppositeDirection" : true, "depth" : 25 * mm});
        }
        {
            var Q0;
            {var subQ0=sQuery(id+"F0.wireOp",EDGE,"E13");var subQ1=sQuery(id+"F0.wireOp",EDGE,"E14");var subQ2=sQuery(id+"F0.wireOp",EDGE,"E16.0");var subQ3=sQuery(id+"F0.wireOp",EDGE,"E18");var subQ4=sQuery(id+"F0.wireOp",EDGE,"E52");var subQ5=sQuery(id+"F0.wireOp",EDGE,"E53");Q0=makeQuery(id+"F17.boolean.opBoolean","SPLIT",FACE,{"disambiguationData":[TD([makeQuery(id+"F7.opExtrude","SWEPT_FACE",FACE,{"disambiguationData":[OSD([subQ0])]})])],"derivedFrom":makeQuery(id+"F7.opExtrude","CAP_FACE",FACE,{"disambiguationData":[OSD([sQuery(id+"F0.wireOp",EDGE,"E0.rect.left"),sQuery(id+"F0.wireOp",EDGE,"E0.rect.right"),sQuery(id+"F0.wireOp",EDGE,"E2"),sQuery(id+"F0.wireOp",EDGE,"E4"),sQuery(id+"F0.wireOp",EDGE,"E5"),sQuery(id+"F0.wireOp",EDGE,"E6"),sQuery(id+"F0.wireOp",EDGE,"E8"),sQuery(id+"F0.wireOp",EDGE,"E9.trimOffspring"),sQuery(id+"F0.wireOp",EDGE,"E11"),subQ0,subQ1,sQuery(id+"F0.wireOp",EDGE,"E15"),subQ2,sQuery(id+"F0.wireOp",EDGE,"E17"),subQ3,sQuery(id+"F0.wireOp",EDGE,"E19"),sQuery(id+"F0.wireOp",EDGE,"E20"),sQuery(id+"F0.wireOp",EDGE,"E22"),sQuery(id+"F0.wireOp",EDGE,"E23"),sQuery(id+"F0.wireOp",EDGE,"E26"),sQuery(id+"F0.wireOp",EDGE,"E32"),sQuery(id+"F0.wireOp",EDGE,"E33"),sQuery(id+"F0.wireOp",EDGE,"E34"),sQuery(id+"F0.wireOp",EDGE,"E35"),sQuery(id+"F0.wireOp",EDGE,"E36"),sQuery(id+"F0.wireOp",EDGE,"E37"),sQuery(id+"F0.wireOp",EDGE,"E39.MirrorCS"),sQuery(id+"F0.wireOp",EDGE,"E40.MirrorCS"),sQuery(id+"F0.wireOp",EDGE,"E41.MirrorCS"),sQuery(id+"F0.wireOp",EDGE,"E42.MirrorCS"),sQuery(id+"F0.wireOp",EDGE,"E43.MirrorCS"),sQuery(id+"F0.wireOp",EDGE,"E44.MirrorCS"),sQuery(id+"F0.wireOp",EDGE,"E45.trimOffspring"),sQuery(id+"F0.wireOp",EDGE,"E46"),sQuery(id+"F0.wireOp",EDGE,"E48"),sQuery(id+"F0.wireOp",EDGE,"E50"),subQ4,subQ5])],"isStart":true})});}
            var sketch = newSketch(context, id + "F25", { "sketchPlane" : qUnion([Q0])});
            skLineSegment(sketch, "E111.0", {"start": v(9.05, 22.9) * mm, "end": v(12.25, 22.9) * mm, "construction": true});
            skLineSegment(sketch, "E112.0", {"start": v(9.05, 16.7) * mm, "end": v(12.25, 16.7) * mm, "construction": true});
            skLineSegment(sketch, "E113", {"start": v(12.25, 22.9) * mm, "end": v(12.25, 16.7) * mm, "construction": true});
            skLineSegment(sketch, "E114", {"start": v(12.25, 19.8) * mm, "end": v(15.1, 19.8) * mm, "construction": true});
            skLineSegment(sketch, "E115.rect.bottom", {"start": v(15.1, 21.4) * mm, "end": v(9.4, 21.4) * mm});
            skLineSegment(sketch, "E115.rect.top", {"start": v(15.1, 18.2) * mm, "end": v(9.4, 18.2) * mm});
            skLineSegment(sketch, "E115.rect.left", {"start": v(15.1, 21.4) * mm, "end": v(15.1, 18.2) * mm});
            skLineSegment(sketch, "E115.rect.right", {"start": v(9.4, 21.4) * mm, "end": v(9.4, 18.2) * mm});
            skPoint(sketch, "E115.rect.middle", {"position": v(12.25, 19.8) * mm});
            skSolve(sketch);
        }
        {
            var Q0;
            Q0 = qSketchRegion(id + "F25", true);
            extrude(context, id + "F26", {"entities" : qUnion([Q0]), "operationType" : NewBodyOperationType.REMOVE, "oppositeDirection" : true, "depth" : 25 * mm});
        }
        {
            var Q0;
            {var subQ0=sQuery(id+"F0.wireOp",EDGE,"E0.rect.left");var subQ1=sQuery(id+"F0.wireOp",EDGE,"E0.rect.right");var subQ2=sQuery(id+"F0.wireOp",EDGE,"E2");var subQ3=sQuery(id+"F0.wireOp",EDGE,"E4");var subQ4=sQuery(id+"F0.wireOp",EDGE,"E5");var subQ5=sQuery(id+"F0.wireOp",EDGE,"E6");var subQ6=sQuery(id+"F0.wireOp",EDGE,"E8");var subQ7=sQuery(id+"F0.wireOp",EDGE,"E9.trimOffspring");var subQ8=sQuery(id+"F0.wireOp",EDGE,"E11");var subQ9=sQuery(id+"F0.wireOp",EDGE,"E13");var subQ10=sQuery(id+"F0.wireOp",EDGE,"E14");var subQ11=sQuery(id+"F0.wireOp",EDGE,"E15");var subQ12=sQuery(id+"F0.wireOp",EDGE,"E16.0");var subQ13=sQuery(id+"F0.wireOp",EDGE,"E17");var subQ14=sQuery(id+"F0.wireOp",EDGE,"E18");var subQ15=sQuery(id+"F0.wireOp",EDGE,"E19");var subQ16=sQuery(id+"F0.wireOp",EDGE,"E20");var subQ17=sQuery(id+"F0.wireOp",EDGE,"E22");var subQ18=sQuery(id+"F0.wireOp",EDGE,"E23");var subQ19=sQuery(id+"F0.wireOp",EDGE,"E26");var subQ20=sQuery(id+"F0.wireOp",EDGE,"E32");var subQ21=sQuery(id+"F0.wireOp",EDGE,"E33");var subQ22=sQuery(id+"F0.wireOp",EDGE,"E34");var subQ23=sQuery(id+"F0.wireOp",EDGE,"E35");var subQ24=sQuery(id+"F0.wireOp",EDGE,"E36");var subQ25=sQuery(id+"F0.wireOp",EDGE,"E37");var subQ26=sQuery(id+"F0.wireOp",EDGE,"E39.MirrorCS");var subQ27=sQuery(id+"F0.wireOp",EDGE,"E40.MirrorCS");var subQ28=sQuery(id+"F0.wireOp",EDGE,"E41.MirrorCS");var subQ29=sQuery(id+"F0.wireOp",EDGE,"E42.MirrorCS");var subQ30=sQuery(id+"F0.wireOp",EDGE,"E43.MirrorCS");var subQ31=sQuery(id+"F0.wireOp",EDGE,"E44.MirrorCS");var subQ32=sQuery(id+"F0.wireOp",EDGE,"E45.trimOffspring");var subQ33=sQuery(id+"F0.wireOp",EDGE,"E46");var subQ34=sQuery(id+"F0.wireOp",EDGE,"E48");var subQ35=sQuery(id+"F0.wireOp",EDGE,"E50");var subQ36=sQuery(id+"F0.wireOp",EDGE,"E52");var subQ37=sQuery(id+"F0.wireOp",EDGE,"E53");Q0=makeQuery(id+"F17.boolean.opBoolean","SPLIT",FACE,{"disambiguationData":[TD([makeQuery(id+"F7.opExtrude","SWEPT_FACE",FACE,{"disambiguationData":[OSD([subQ0])]})])],"derivedFrom":makeQuery(id+"F7.opExtrude","CAP_FACE",FACE,{"disambiguationData":[OSD([subQ0,subQ1,subQ2,subQ3,subQ4,subQ5,subQ6,subQ7,subQ8,subQ9,subQ10,subQ11,subQ12,subQ13,subQ14,subQ15,subQ16,subQ17,subQ18,subQ19,subQ20,subQ21,subQ22,subQ23,subQ24,subQ25,subQ26,subQ27,subQ28,subQ29,subQ30,subQ31,subQ32,subQ33,subQ34,subQ35,subQ36,subQ37])],"isStart":true})});}
            var sketch = newSketch(context, id + "F27", { "sketchPlane" : qUnion([Q0])});
            skLineSegment(sketch, "E116.0", {"start": v(0.1, 14.58) * mm, "end": v(0.1, 3.86) * mm, "construction": true});
            skLineSegment(sketch, "E117.0", {"start": v(3.1, 25.2) * mm, "end": v(3.1, 2.33) * mm, "construction": true});
            skLineSegment(sketch, "E118.bottom", {"start": v(0.1, 9.22) * mm, "end": v(3.1, 9.22) * mm});
            skLineSegment(sketch, "E118.top", {"start": v(0.1, -19.81) * mm, "end": v(3.1, -19.81) * mm});
            skLineSegment(sketch, "E118.left", {"start": v(0.1, 9.22) * mm, "end": v(0.1, -19.81) * mm});
            skLineSegment(sketch, "E118.right", {"start": v(3.1, 9.22) * mm, "end": v(3.1, -19.81) * mm});
            skSolve(sketch);
        }
        {
            var Q0;
            Q0 = qSketchRegion(id + "F27", true);
            extrude(context, id + "F28", {"entities" : qUnion([Q0]), "operationType" : NewBodyOperationType.REMOVE, "oppositeDirection" : true, "depth" : 25 * mm});
        }
        {
            var Q0;
            Q0=makeQuery(id+"F28.boolean.opBoolean","INTERSECT",EDGE,{"derivedFrom":[makeQuery(id+"F7.opExtrude","SWEPT_FACE",FACE,{"disambiguationData":[OSD([sQuery(id+"F0.wireOp",EDGE,"E4")])]}),makeQuery(id+"F28.opExtrude","SWEPT_FACE",FACE,{"disambiguationData":[OSD([sQuery(id+"F27.wireOp",EDGE,"E118.left")])]})]});
            var Q1;
            Q1=makeQuery(id+"F28.boolean.opBoolean","INTERSECT",EDGE,{"derivedFrom":[makeQuery(id+"F7.opExtrude","SWEPT_FACE",FACE,{"disambiguationData":[OSD([sQuery(id+"F0.wireOp",EDGE,"E8")])]}),makeQuery(id+"F28.opExtrude","SWEPT_FACE",FACE,{"disambiguationData":[OSD([sQuery(id+"F27.wireOp",EDGE,"E118.right")])]})]});
            chamfer(context, id + "F29", {"entities" : qUnion([Q0, Q1]), "chamferType" : ChamferType.TWO_OFFSETS, "width1" : 3 * mm, "oppositeDirection" : false, "width2" : 5 * mm, "tangentPropagation" : true});
        }
        {
            var Q0;
            {var subQ0=makeQuery(id+"F28.opExtrude","SWEPT_FACE",FACE,{"disambiguationData":[OSD([sQuery(id+"F27.wireOp",EDGE,"E118.right")])]});Q0=makeQuery(id+"F29.opChamfer","BLEND_EDGE",EDGE,{"blendedFrom":[makeQuery(id+"F28.boolean.opBoolean","INTERSECT",EDGE,{"derivedFrom":[makeQuery(id+"F7.opExtrude","SWEPT_FACE",FACE,{"disambiguationData":[OSD([sQuery(id+"F0.wireOp",EDGE,"E8")])]}),subQ0]}),makeQuery(id+"F28.boolean.opBoolean","COPY",FACE,{"derivedFrom":subQ0})],"blendedInto":[makeQuery(id+"F28.boolean.opBoolean","COPY",FACE,{"derivedFrom":subQ0})]});}
            chamfer(context, id + "F30", {"entities" : qUnion([Q0]), "chamferType" : ChamferType.TWO_OFFSETS, "width1" : 3 * mm, "oppositeDirection" : false, "width2" : 2 * mm, "tangentPropagation" : true});
        }
        {
            var Q0;
            {var subQ0=makeQuery(id+"F7.opExtrude","SWEPT_FACE",FACE,{"disambiguationData":[OSD([sQuery(id+"F0.wireOp",EDGE,"E4")])]});Q0=makeQuery(id+"F29.opChamfer","BLEND_EDGE",EDGE,{"blendedFrom":[makeQuery(id+"F28.boolean.opBoolean","INTERSECT",EDGE,{"derivedFrom":[subQ0,makeQuery(id+"F28.opExtrude","SWEPT_FACE",FACE,{"disambiguationData":[OSD([sQuery(id+"F27.wireOp",EDGE,"E118.left")])]})]}),subQ0],"blendedInto":[subQ0]});}
            var Q1;
            {var subQ0=makeQuery(id+"F28.opExtrude","SWEPT_FACE",FACE,{"disambiguationData":[OSD([sQuery(id+"F27.wireOp",EDGE,"E118.left")])]});Q1=makeQuery(id+"F29.opChamfer","BLEND_EDGE",EDGE,{"blendedFrom":[makeQuery(id+"F28.boolean.opBoolean","INTERSECT",EDGE,{"derivedFrom":[makeQuery(id+"F7.opExtrude","SWEPT_FACE",FACE,{"disambiguationData":[OSD([sQuery(id+"F0.wireOp",EDGE,"E4")])]}),subQ0]}),makeQuery(id+"F28.boolean.opBoolean","COPY",FACE,{"derivedFrom":subQ0})],"blendedInto":[makeQuery(id+"F28.boolean.opBoolean","COPY",FACE,{"derivedFrom":subQ0})]});}
            var Q2;
            {var subQ0=makeQuery(id+"F28.opExtrude","SWEPT_FACE",FACE,{"disambiguationData":[OSD([sQuery(id+"F27.wireOp",EDGE,"E118.right")])]});var subQ1=makeQuery(id+"F28.boolean.opBoolean","COPY",FACE,{"derivedFrom":subQ0});Q2=makeQuery(id+"F30.opChamfer","BLEND_EDGE",EDGE,{"blendedFrom":[makeQuery(id+"F29.opChamfer","BLEND_EDGE",EDGE,{"blendedFrom":[makeQuery(id+"F28.boolean.opBoolean","INTERSECT",EDGE,{"derivedFrom":[makeQuery(id+"F7.opExtrude","SWEPT_FACE",FACE,{"disambiguationData":[OSD([sQuery(id+"F0.wireOp",EDGE,"E8")])]}),subQ0]}),subQ1],"blendedInto":[subQ1]}),subQ1],"blendedInto":[subQ1]});}
            var Q3;
            {var subQ0=sQuery(id+"F0.wireOp",EDGE,"E8");var subQ1=sQuery(id+"F27.wireOp",EDGE,"E118.right");var subQ2=makeQuery(id+"F28.opExtrude","SWEPT_FACE",FACE,{"disambiguationData":[OSD([subQ1])]});Q3=makeQuery(id+"F30.opChamfer","BLEND_EDGE",EDGE,{"blendedFrom":[makeQuery(id+"F29.opChamfer","BLEND_EDGE",EDGE,{"blendedFrom":[makeQuery(id+"F28.boolean.opBoolean","INTERSECT",EDGE,{"derivedFrom":[makeQuery(id+"F7.opExtrude","SWEPT_FACE",FACE,{"disambiguationData":[OSD([subQ0])]}),subQ2]}),makeQuery(id+"F28.boolean.opBoolean","COPY",FACE,{"derivedFrom":subQ2})],"blendedInto":[makeQuery(id+"F28.boolean.opBoolean","COPY",FACE,{"derivedFrom":subQ2})]}),makeQuery(id+"F29.opChamfer","BLEND_FACE",FACE,{"disambiguationData":[OSD([subQ0,subQ1])]})],"blendedInto":[makeQuery(id+"F29.opChamfer","BLEND_FACE",FACE,{"disambiguationData":[OSD([subQ0,subQ1])]})]});}
            fillet(context, id + "F31", {"entities" : qUnion([Q0, Q1, Q2, Q3]), "radius" : 2 * mm, "tangentPropagation" : true, "allowEdgeOverflow" : false});
        }
        {
            var Q0;
            {var subQ0=sQuery(id+"F0.wireOp",EDGE,"E46");var subQ1=sQuery(id+"F0.wireOp",EDGE,"E0.rect.left");Q0=makeQuery(id+"F22.boolean.opBoolean","SPLIT",FACE,{"disambiguationData":[TD([makeQuery(id+"F7.opExtrude","SWEPT_FACE",FACE,{"disambiguationData":[OSD([subQ1])]})])],"derivedFrom":makeQuery(id+"F7.opExtrude","SWEPT_FACE",FACE,{"disambiguationData":[OSD([subQ0])]})});}
            var sketch = newSketch(context, id + "F32", { "sketchPlane" : qUnion([Q0])});
            skLineSegment(sketch, "E119", {"start": v(-16.33, 0) * mm, "end": v(-13.18, -2.8) * mm, "construction": true});
            skLineSegment(sketch, "E120.0", {"start": v(18.37, -2.85) * mm, "end": v(18.37, 0) * mm, "construction": true});
            skLineSegment(sketch, "E121.0", {"start": v(21.47, -2.85) * mm, "end": v(21.47, 0) * mm, "construction": true});
            skLineSegment(sketch, "E122", {"start": v(18.37, -1.43) * mm, "end": v(21.47, -1.43) * mm, "construction": true});
            skLineSegment(sketch, "E123.0", {"start": v(-13.23, -2.85) * mm, "end": v(-13.23, 0) * mm});
            skLineSegment(sketch, "E124.trimOffspring", {"start": v(-13.23, -1.43) * mm, "end": v(-16.33, -1.43) * mm, "construction": true});
            skPoint(sketch, "E125.orphan", {"position": v(0.08, 0) * mm});
            skPoint(sketch, "E126.0.end.orphan", {"position": v(3.08, -2.85) * mm});
            skPoint(sketch, "E126.0.start.orphan", {"position": v(3.08, 0) * mm});
            skPoint(sketch, "E127.0.end.orphan", {"position": v(0.08, -2.85) * mm});
            skPoint(sketch, "E128", {"position": v(19.92, -1.43) * mm});
            skPoint(sketch, "E129", {"position": v(-14.73, -1.43) * mm});
            skSolve(sketch);
        }
    });
